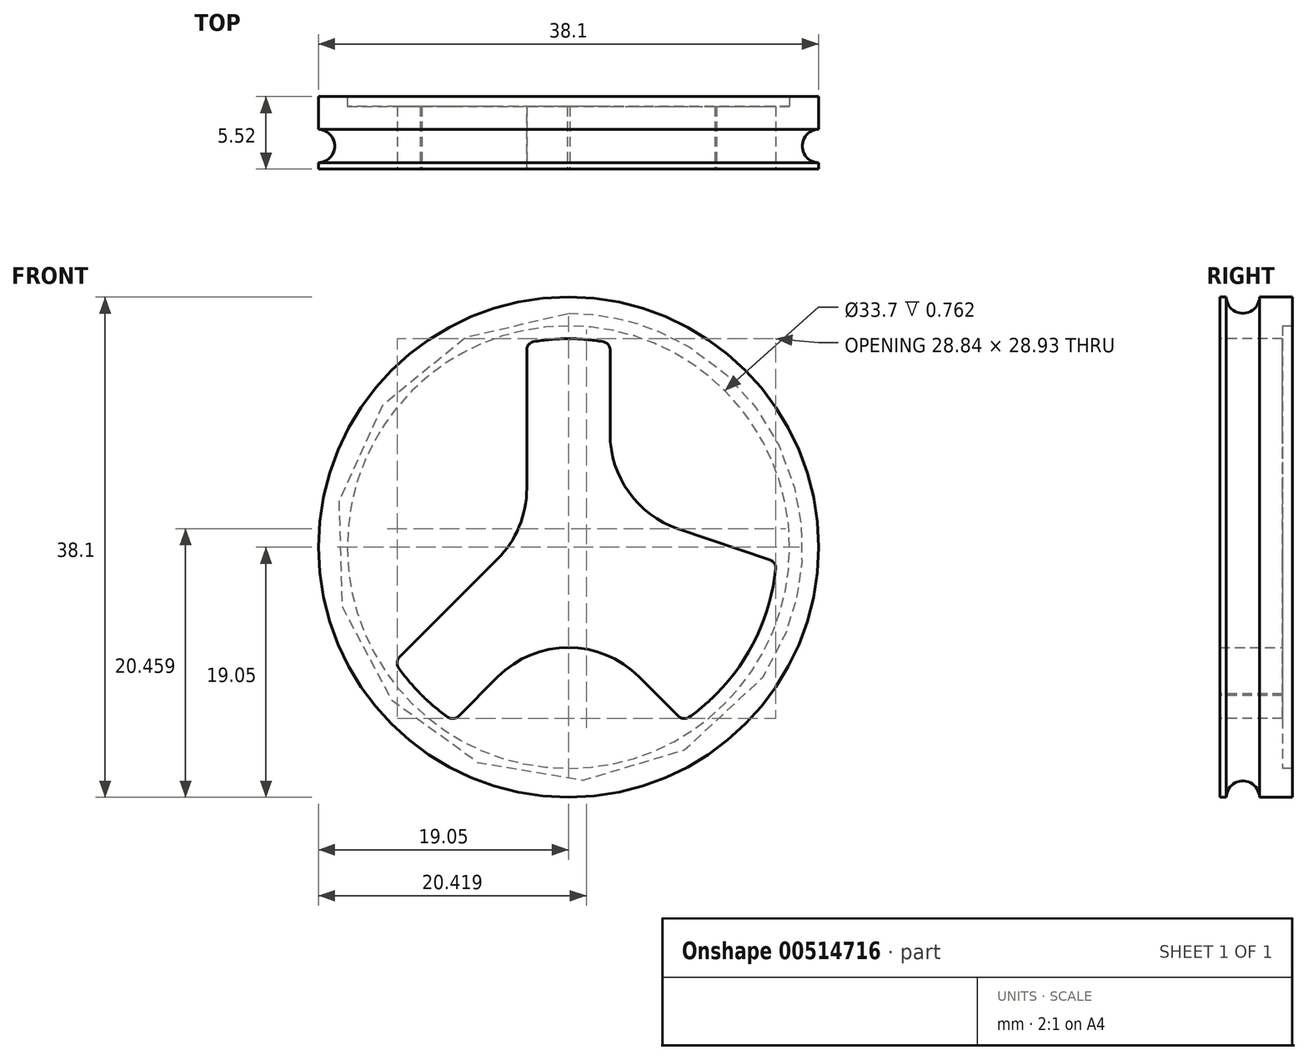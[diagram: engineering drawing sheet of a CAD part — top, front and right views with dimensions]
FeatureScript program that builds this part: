
annotation { "Feature Type Name" : "Feature", "Feature Type Description" : "" }
export const myFeature = defineFeature(function(context is Context, id is Id, definition is map)
    precondition{}
    {
        {
            var Q0;
            Q0=qCreatedBy(makeId("Front.planeOp"),FACE);
            var sketch = newSketch(context, id + "F0", { "sketchPlane" : qUnion([Q0])});
            skCircle(sketch, "E0", {"center": v(0, 0) * mm, "radius": 19.05 * mm});
            skSolve(sketch);
        }
        {
            var Q0;
            Q0=qSketchRegion(id+"F0",true);
            extrude(context, id + "F1", {"entities" : qUnion([Q0]), "depth" : 4.76 * mm});
        }
        {
            var Q0;
            Q0=makeQuery(id+"F1.opExtrude","CAP_FACE",FACE,{"disambiguationData":[OSD([sQuery(id+"F0.wireOp",EDGE,"E0")])],"isStart":false});
            var sketch = newSketch(context, id + "F2", { "sketchPlane" : qUnion([Q0])});
            skArc(sketch, "E1.3.0", {"start": v(-11.29, -11.16) * mm, "mid": v(-11.22, -11.23) * mm, "end": v(-11.16, -11.3) * mm});
            skArc(sketch, "E1.5.0", {"start": v(11.16, -11.29) * mm, "mid": v(11.23, -11.23) * mm, "end": v(11.3, -11.16) * mm});
            skPoint(sketch, "E1.center", {"position": v(0, 0) * mm});
            skLineSegment(sketch, "E2", {"start": v(-2.24, 2.24) * mm, "end": v(-13.32, -8.83) * mm});
            skLineSegment(sketch, "E3", {"start": v(-3.17, 0) * mm, "end": v(-3.18, 15.55) * mm});
            skLineSegment(sketch, "E4", {"start": v(3.18, 3.17) * mm, "end": v(3.17, 15.55) * mm});
            skLineSegment(sketch, "E5", {"start": v(3.17, 15.42) * mm, "end": v(3.1, 15.09) * mm});
            skArc(sketch, "E6", {"start": v(-13.24, -8.76) * mm, "mid": v(-11.22, -11.23) * mm, "end": v(-8.75, -13.25) * mm});
            skArc(sketch, "E7.trimOffspring", {"start": v(0.1, 15.87) * mm, "mid": v(0, 15.87) * mm, "end": v(-0.1, 15.87) * mm});
            skArc(sketch, "E8.trimOffspring", {"start": v(3.17, 15.55) * mm, "mid": v(0, 15.87) * mm, "end": v(-3.18, 15.55) * mm});
            skArc(sketch, "E9.trimOffspring", {"start": v(8.76, -13.24) * mm, "mid": v(14.67, -6.08) * mm, "end": v(15.55, 3.18) * mm});
            skLineSegment(sketch, "E10.trimOffspring", {"start": v(0, -4.5) * mm, "end": v(8.76, -13.24) * mm});
            skLineSegment(sketch, "E11.trimOffspring", {"start": v(0, -4.5) * mm, "end": v(-8.75, -13.25) * mm});
            skArc(sketch, "E12.trimOffspring", {"start": v(-2.24, 2.24) * mm, "mid": v(-2.93, 1.21) * mm, "end": v(-3.17, 0) * mm});
            skPoint(sketch, "E13.end.orphan", {"position": v(3.18, 0) * mm});
            skLineSegment(sketch, "E14", {"start": v(3.18, 3.17) * mm, "end": v(15.83, -1.15) * mm});
            skSolve(sketch);
        }
        {
            var Q0;
            Q0=qSketchRegion(id+"F2",true);
            extrude(context, id + "F3", {"entities" : qUnion([Q0]), "operationType" : NewBodyOperationType.REMOVE, "oppositeDirection" : true, "depth" : 25.4 * mm});
        }
        {
            var Q0;
            Q0=makeQuery(id+"F3.boolean.opBoolean","COPY",EDGE,{"derivedFrom":makeQuery(id+"F3.opExtrude","SWEPT_EDGE",EDGE,{"disambiguationData":[OSD([sQuery(id+"F2.wireOp",EDGE,"E2"),sQuery(id+"F2.wireOp",EDGE,"E6")])]})});
            var Q1;
            Q1=makeQuery(id+"F3.boolean.opBoolean","COPY",EDGE,{"derivedFrom":makeQuery(id+"F3.opExtrude","SWEPT_EDGE",EDGE,{"disambiguationData":[OSD([sQuery(id+"F2.wireOp",EDGE,"E6"),sQuery(id+"F2.wireOp",EDGE,"E11.trimOffspring")])]})});
            var Q2;
            Q2=makeQuery(id+"F3.boolean.opBoolean","COPY",EDGE,{"derivedFrom":makeQuery(id+"F3.opExtrude","SWEPT_EDGE",EDGE,{"disambiguationData":[OSD([sQuery(id+"F2.wireOp",EDGE,"E9.trimOffspring"),sQuery(id+"F2.wireOp",EDGE,"E10.trimOffspring")])]})});
            var Q3;
            Q3=makeQuery(id+"F3.boolean.opBoolean","COPY",EDGE,{"derivedFrom":makeQuery(id+"F3.opExtrude","SWEPT_EDGE",EDGE,{"disambiguationData":[OSD([sQuery(id+"F2.wireOp",EDGE,"E9.trimOffspring"),sQuery(id+"F2.wireOp",EDGE,"E14")])]})});
            var Q4;
            Q4=makeQuery(id+"F3.boolean.opBoolean","COPY",EDGE,{"derivedFrom":makeQuery(id+"F3.opExtrude","SWEPT_EDGE",EDGE,{"disambiguationData":[OSD([sQuery(id+"F2.wireOp",EDGE,"E4"),sQuery(id+"F2.wireOp",EDGE,"E8.trimOffspring")])]})});
            var Q5;
            Q5=makeQuery(id+"F3.boolean.opBoolean","COPY",EDGE,{"derivedFrom":makeQuery(id+"F3.opExtrude","SWEPT_EDGE",EDGE,{"disambiguationData":[OSD([sQuery(id+"F2.wireOp",EDGE,"E3"),sQuery(id+"F2.wireOp",EDGE,"E8.trimOffspring")])]})});
            fillet(context, id + "F4", {"entities" : qUnion([Q0, Q1, Q2, Q3, Q4, Q5]), "radius" : 0.64 * mm, "tangentPropagation" : true, "allowEdgeOverflow" : false});
        }
        {
            var Q0;
            Q0=makeQuery(id+"F3.boolean.opBoolean","COPY",EDGE,{"derivedFrom":makeQuery(id+"F3.opExtrude","SWEPT_EDGE",EDGE,{"disambiguationData":[OSD([sQuery(id+"F2.wireOp",EDGE,"E2"),sQuery(id+"F2.wireOp",EDGE,"E3")])]})});
            var Q1;
            Q1=makeQuery(id+"F3.boolean.opBoolean","COPY",EDGE,{"derivedFrom":makeQuery(id+"F3.opExtrude","SWEPT_EDGE",EDGE,{"disambiguationData":[OSD([sQuery(id+"F2.wireOp",EDGE,"E10.trimOffspring"),sQuery(id+"F2.wireOp",EDGE,"E11.trimOffspring")])]})});
            var Q2;
            Q2=makeQuery(id+"F3.boolean.opBoolean","COPY",EDGE,{"derivedFrom":makeQuery(id+"F3.opExtrude","SWEPT_EDGE",EDGE,{"disambiguationData":[OSD([sQuery(id+"F2.wireOp",EDGE,"E4"),sQuery(id+"F2.wireOp",EDGE,"E14")])]})});
            fillet(context, id + "F5", {"entities" : qUnion([Q0, Q1, Q2]), "radius" : 7.62 * mm, "tangentPropagation" : true, "allowEdgeOverflow" : false});
        }
        {
            var Q0;
            Q0=makeQuery(id+"F1.opExtrude","CAP_FACE",FACE,{"disambiguationData":[OSD([sQuery(id+"F0.wireOp",EDGE,"E0")])],"isStart":true});
            var sketch = newSketch(context, id + "F6", { "sketchPlane" : qUnion([Q0])});
            skCircle(sketch, "E15", {"center": v(0, 0) * mm, "radius": 19.05 * mm});
            skCircle(sketch, "E16", {"center": v(0, 0) * mm, "radius": 16.85 * mm});
            skSolve(sketch);
        }
        {
            var Q0;
            Q0=qSketchRegion(id+"F6",true);
            extrude(context, id + "F7", {"entities" : qUnion([Q0]), "operationType" : NewBodyOperationType.ADD, "depth" : 0.76 * mm});
        }
        {
            var Q0;
            Q0=qCreatedBy(makeId("Top.planeOp"),FACE);
            var sketch = newSketch(context, id + "F8", { "sketchPlane" : qUnion([Q0])});
            skCircle(sketch, "E17", {"center": v(-19.08, -3) * mm, "radius": 1.27 * mm});
            skSolve(sketch);
        }
        {
            var Q0;
            Q0=qSketchRegion(id+"F8",true);
            var Q1;
            Q1=makeQuery(id+"F7.opExtrude","CAP_EDGE",EDGE,{"disambiguationData":[OSD([sQuery(id+"F6.wireOp",EDGE,"E16")])],"isStart":false});
            revolve(context, id + "F9", {"operationType" : NewBodyOperationType.REMOVE, "entities" : qUnion([Q0]), "axis" : qUnion([Q1]), "revolveType" : RevolveType.FULL, "oppositeDirection" : true});
        }
    });
